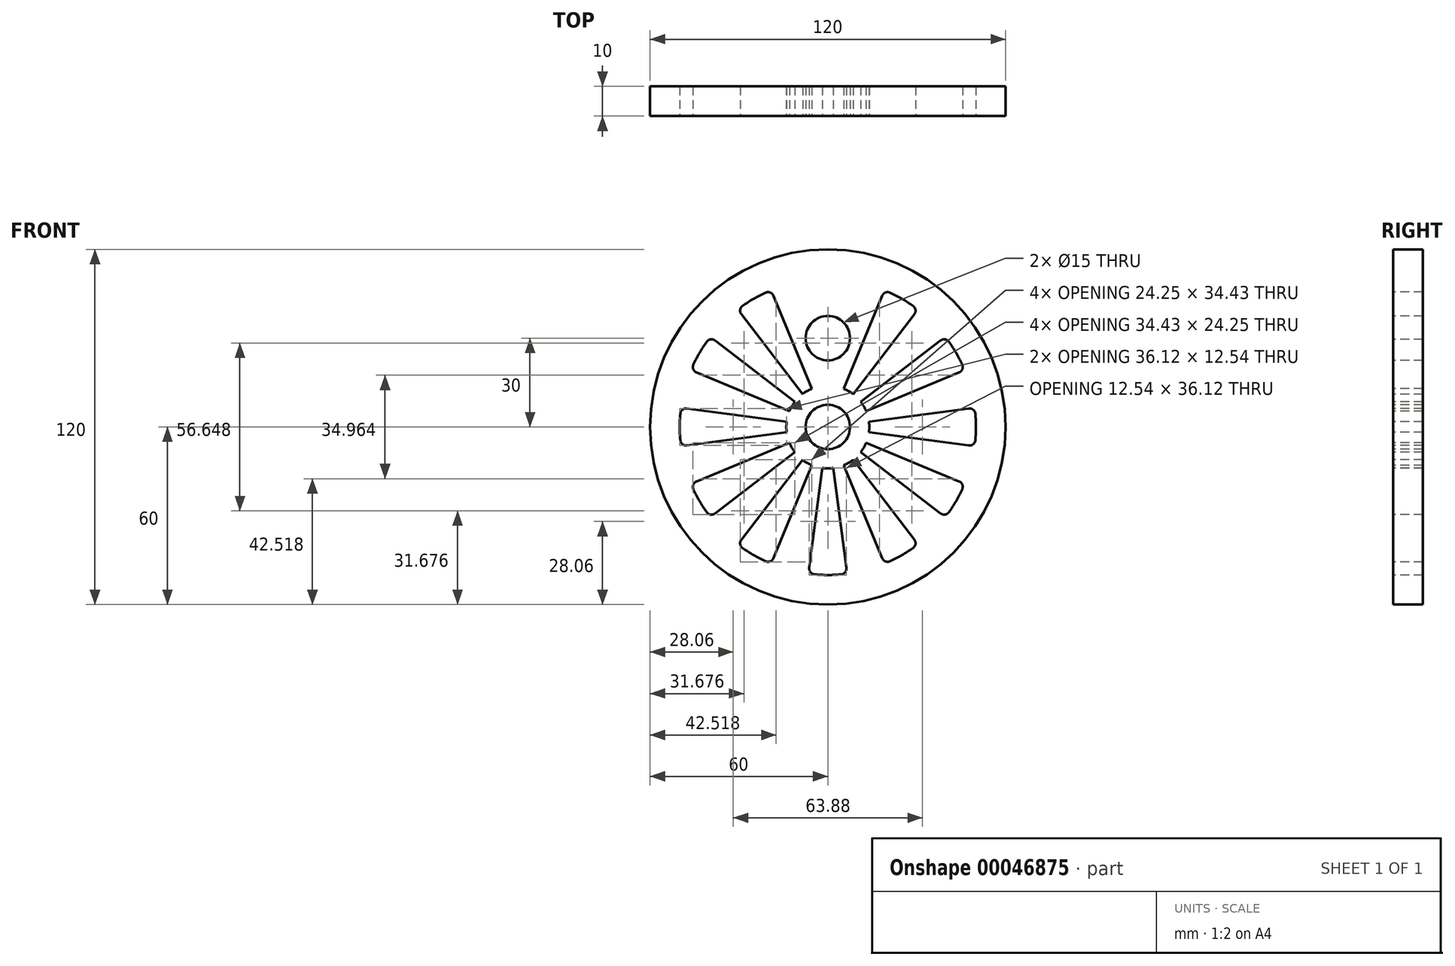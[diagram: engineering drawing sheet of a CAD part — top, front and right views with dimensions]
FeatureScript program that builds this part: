
annotation { "Feature Type Name" : "Feature", "Feature Type Description" : "" }
export const myFeature = defineFeature(function(context is Context, id is Id, definition is map)
    precondition{}
    {
        {
            var Q0;
            Q0=qCreatedBy(makeId("Front.planeOp"),FACE);
            var sketch = newSketch(context, id + "F0", { "sketchPlane" : qUnion([Q0])});
            skCircle(sketch, "E0", {"center": v(0, 0) * mm, "radius": 60 * mm});
            skSolve(sketch);
        }
        {
            var Q0;
            Q0 = qSketchRegion(id + "F0", true);
            extrude(context, id + "F1", {"entities" : qUnion([Q0]), "depth" : 10 * mm});
        }
        {
            var Q0;
            Q0=makeQuery(id+"F1.opExtrude","CAP_FACE",FACE,{"disambiguationData":[OSD([sQuery(id+"F0.wireOp",EDGE,"E0")])],"isStart":false});
            var sketch = newSketch(context, id + "F2", { "sketchPlane" : qUnion([Q0])});
            skCircle(sketch, "E1", {"center": v(0, 0) * mm, "radius": 7.5 * mm});
            skSolve(sketch);
        }
        {
            var Q0;
            Q0 = qSketchRegion(id + "F2", true);
            extrude(context, id + "F3", {"entities" : qUnion([Q0]), "operationType" : NewBodyOperationType.REMOVE, "endBound" : BoundingType.THROUGH_ALL, "oppositeDirection" : true, "depth" : 25 * mm});
        }
        {
            var Q0;
            Q0=makeQuery(id+"F1.opExtrude","CAP_FACE",FACE,{"disambiguationData":[OSD([sQuery(id+"F0.wireOp",EDGE,"E0")])],"isStart":false});
            var sketch = newSketch(context, id + "F4", { "sketchPlane" : qUnion([Q0])});
            skArc(sketch, "E2", {"start": v(-1.83, 13.88) * mm, "mid": v(0, 14) * mm, "end": v(1.83, 13.88) * mm});
            skArc(sketch, "E3", {"start": v(-6.53, 49.57) * mm, "mid": v(0, 50) * mm, "end": v(6.53, 49.57) * mm});
            skLineSegment(sketch, "E4", {"start": v(-6.53, 49.57) * mm, "end": v(-1.83, 13.88) * mm});
            skLineSegment(sketch, "E5", {"start": v(6.53, 49.57) * mm, "end": v(1.83, 13.88) * mm});
            skLineSegment(sketch, "E6", {"start": v(6.53, 49.57) * mm, "end": v(0, 0) * mm, "construction": true});
            skLineSegment(sketch, "E7", {"start": v(-6.53, 49.57) * mm, "end": v(0, 0) * mm, "construction": true});
            skLineSegment(sketch, "E8", {"start": v(0, 0) * mm, "end": v(0, 50) * mm, "construction": true});
            skSolve(sketch);
        }
        {
            var Q0;
            Q0 = qSketchRegion(id + "F4", true);
            extrude(context, id + "F5", {"entities" : qUnion([Q0]), "operationType" : NewBodyOperationType.REMOVE, "endBound" : BoundingType.THROUGH_ALL, "oppositeDirection" : true, "depth" : 25 * mm});
        }
        {
            var Q0;
            Q0=makeQuery(id+"F5.boolean.opBoolean","COPY",EDGE,{"derivedFrom":makeQuery(id+"F5.opExtrude","SWEPT_EDGE",EDGE,{"disambiguationData":[OSD([sQuery(id+"F4.wireOp",EDGE,"E3"),sQuery(id+"F4.wireOp",EDGE,"E4")])]})});
            var Q1;
            Q1=makeQuery(id+"F5.boolean.opBoolean","COPY",EDGE,{"derivedFrom":makeQuery(id+"F5.opExtrude","SWEPT_EDGE",EDGE,{"disambiguationData":[OSD([sQuery(id+"F4.wireOp",EDGE,"E3"),sQuery(id+"F4.wireOp",EDGE,"E5")])]})});
            fillet(context, id + "F6", {"entities" : qUnion([Q0, Q1]), "radius" : 2 * mm, "tangentPropagation" : true, "allowEdgeOverflow" : false});
        }
        {
            var Q0;
            Q0=makeQuery(id+"F5.boolean.opBoolean","COPY",FACE,{"derivedFrom":makeQuery(id+"F5.opExtrude","SWEPT_FACE",FACE,{"disambiguationData":[OSD([sQuery(id+"F4.wireOp",EDGE,"E4")])]})});
            var Q1;
            Q1=makeQuery(id+"F5.boolean.opBoolean","COPY",FACE,{"derivedFrom":makeQuery(id+"F5.opExtrude","SWEPT_FACE",FACE,{"disambiguationData":[OSD([sQuery(id+"F4.wireOp",EDGE,"E3")])]})});
            var Q2;
            Q2=makeQuery(id+"F5.boolean.opBoolean","COPY",FACE,{"derivedFrom":makeQuery(id+"F5.opExtrude","SWEPT_FACE",FACE,{"disambiguationData":[OSD([sQuery(id+"F4.wireOp",EDGE,"E5")])]})});
            var Q3;
            Q3=makeQuery(id+"F5.boolean.opBoolean","COPY",FACE,{"derivedFrom":makeQuery(id+"F5.opExtrude","SWEPT_FACE",FACE,{"disambiguationData":[OSD([sQuery(id+"F4.wireOp",EDGE,"E2")])]})});
            var Q4;
            Q4=makeQuery(id+"F6.opFillet","BLEND_FACE",FACE,{"disambiguationData":[OSD([sQuery(id+"F4.wireOp",EDGE,"E3"),sQuery(id+"F4.wireOp",EDGE,"E4")])]});
            var Q5;
            Q5=makeQuery(id+"F6.opFillet","BLEND_FACE",FACE,{"disambiguationData":[OSD([sQuery(id+"F4.wireOp",EDGE,"E3"),sQuery(id+"F4.wireOp",EDGE,"E5")])]});
            var Q6;
            Q6=makeQuery(id+"F3.boolean.opBoolean","COPY",FACE,{"derivedFrom":makeQuery(id+"F3.opExtrude","SWEPT_FACE",FACE,{"disambiguationData":[OSD([sQuery(id+"F2.wireOp",EDGE,"E1")])]})});
            circularPattern(context, id + "F7", {"operationType" : NewBodyOperationType.REMOVE, "faces" : qUnion([Q0, Q1, Q2, Q3, Q4, Q5]), "axis" : qUnion([Q6]), "angle" : 360 * degree, "instanceCount" : 12, "equalSpace" : true, "patternType" : PatternType.FACE});
        }
        {
            var Q0;
            Q0 = qSketchRegion(id + "F4", true);
            var Q1;
            Q1=makeQuery(id+"F1.opExtrude","CAP_FACE",FACE,{"disambiguationData":[OSD([sQuery(id+"F0.wireOp",EDGE,"E0")])],"isStart":true});
            extrude(context, id + "F8", {"entities" : qUnion([Q0]), "operationType" : NewBodyOperationType.ADD, "endBound" : BoundingType.UP_TO_SURFACE, "oppositeDirection" : true, "endBoundEntityFace" : qUnion([Q1]), "depth" : 25 * mm});
        }
        {
            var Q0;
            Q0=makeQuery(id+"F8.boolean.opBoolean","MERGE",FACE,{"derivedFrom":[makeQuery(id+"F1.opExtrude","CAP_FACE",FACE,{"disambiguationData":[OSD([sQuery(id+"F0.wireOp",EDGE,"E0")])],"isStart":false}),makeQuery(id+"F8.opExtrude","CAP_FACE",FACE,{"disambiguationData":[OSD([sQuery(id+"F4.wireOp",EDGE,"E2"),sQuery(id+"F4.wireOp",EDGE,"E3"),sQuery(id+"F4.wireOp",EDGE,"E4"),sQuery(id+"F4.wireOp",EDGE,"E5")])],"isStart":true})]});
            var sketch = newSketch(context, id + "F9", { "sketchPlane" : qUnion([Q0])});
            skCircle(sketch, "E9", {"center": v(0, 30) * mm, "radius": 7.5 * mm});
            skLineSegment(sketch, "E10", {"start": v(0, 60) * mm, "end": v(0, 0) * mm, "construction": true});
            skSolve(sketch);
        }
        {
            var Q0;
            Q0 = qSketchRegion(id + "F9", true);
            extrude(context, id + "F10", {"entities" : qUnion([Q0]), "operationType" : NewBodyOperationType.REMOVE, "endBound" : BoundingType.THROUGH_ALL, "oppositeDirection" : true, "depth" : 25 * mm});
        }
    });
